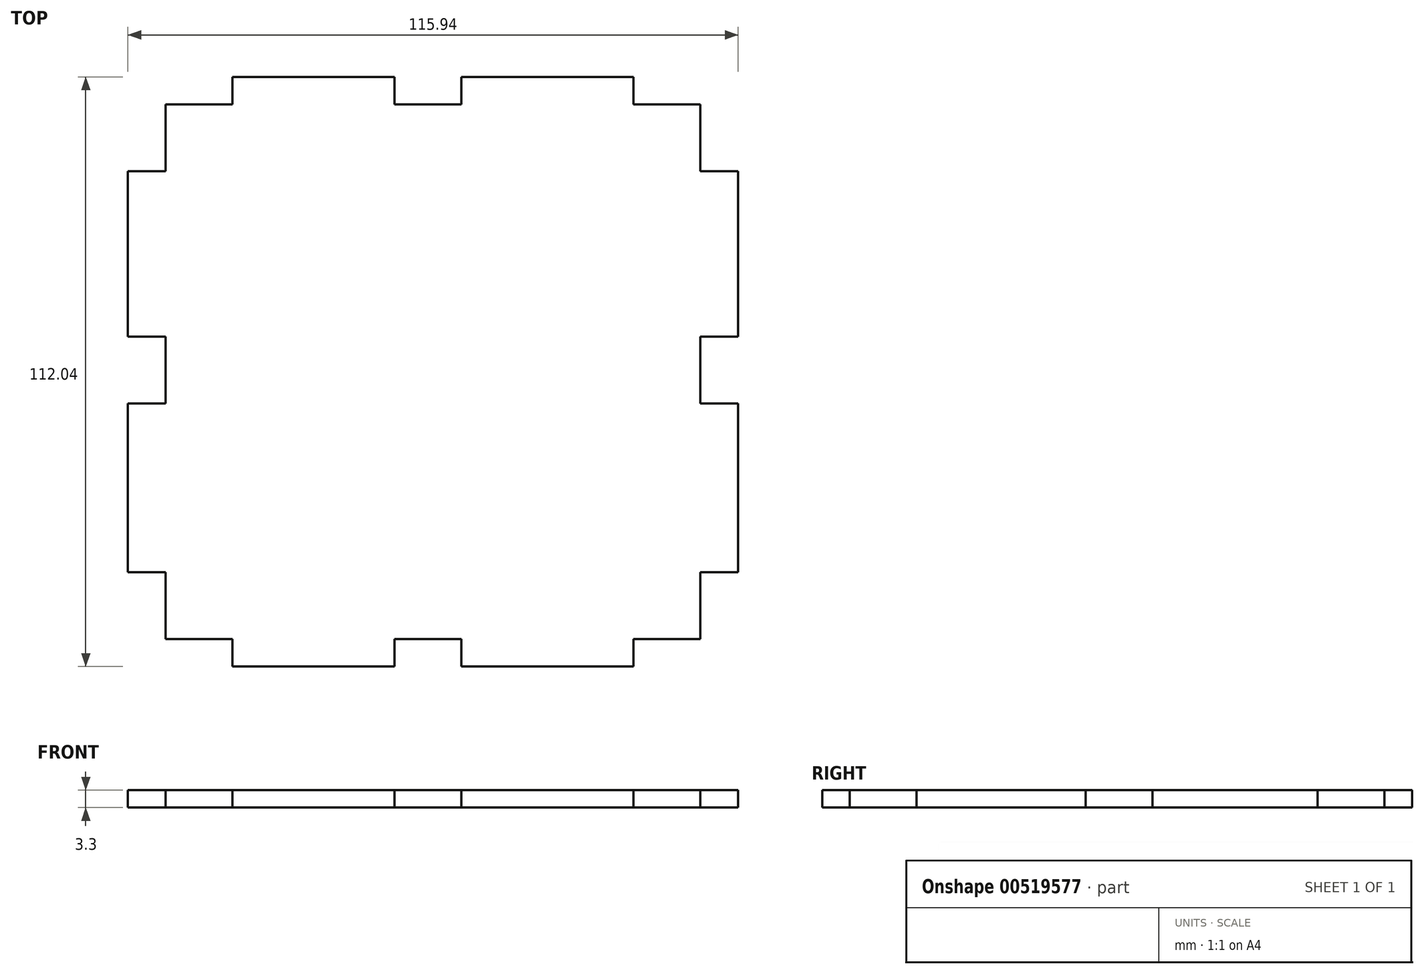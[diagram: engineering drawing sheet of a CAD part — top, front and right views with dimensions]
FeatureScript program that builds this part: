
annotation { "Feature Type Name" : "Feature", "Feature Type Description" : "" }
export const myFeature = defineFeature(function(context is Context, id is Id, definition is map)
    precondition{}
    {
        {
            var Q0;
            Q0=qCreatedBy(makeId("Top.planeOp"),FACE);
            var sketch = newSketch(context, id + "F0", { "sketchPlane" : qUnion([Q0])});
            skLineSegment(sketch, "E0.bottom", {"start": v(50.8, -50.8) * mm, "end": v(38.1, -50.8) * mm});
            skLineSegment(sketch, "E0.top", {"start": v(50.8, 50.8) * mm, "end": v(38.1, 50.8) * mm});
            skLineSegment(sketch, "E0.left", {"start": v(50.8, -50.8) * mm, "end": v(50.8, -38.1) * mm});
            skLineSegment(sketch, "E0.right", {"start": v(-50.8, -50.8) * mm, "end": v(-50.8, -38.1) * mm});
            skPoint(sketch, "E0.middle", {"position": v(0, 0) * mm});
            skLineSegment(sketch, "E1", {"start": v(-50.8, 50.8) * mm, "end": v(-50.8, 56.02) * mm, "construction": true});
            skLineSegment(sketch, "E2", {"start": v(-50.8, 56.02) * mm, "end": v(-38.1, 56.02) * mm, "construction": true});
            skLineSegment(sketch, "E3", {"start": v(-38.1, 56.02) * mm, "end": v(-38.1, 50.8) * mm, "construction": true});
            skLineSegment(sketch, "E4", {"start": v(-38.1, 56.02) * mm, "end": v(-7.3, 56.02) * mm});
            skLineSegment(sketch, "E5", {"start": v(-38.1, 56.02) * mm, "end": v(-38.1, 50.8) * mm});
            skLineSegment(sketch, "E6", {"start": v(-7.3, 56.02) * mm, "end": v(-7.3, 50.8) * mm});
            skLineSegment(sketch, "E7.trimOffspring", {"start": v(-38.1, 50.8) * mm, "end": v(-50.8, 50.8) * mm});
            skLineSegment(sketch, "E8.MirrorCS", {"start": v(-38.1, -56.02) * mm, "end": v(-7.3, -56.02) * mm});
            skLineSegment(sketch, "E9.MirrorCS", {"start": v(-38.1, -56.02) * mm, "end": v(-38.1, -50.8) * mm});
            skLineSegment(sketch, "E10.MirrorCS", {"start": v(-7.3, -56.02) * mm, "end": v(-7.3, -50.8) * mm});
            skLineSegment(sketch, "E11.trimOffspring", {"start": v(-38.1, -50.8) * mm, "end": v(-50.8, -50.8) * mm});
            skLineSegment(sketch, "E12", {"start": v(-7.3, 56.02) * mm, "end": v(5.4, 56.02) * mm, "construction": true});
            skLineSegment(sketch, "E13", {"start": v(5.4, 56.02) * mm, "end": v(5.4, 50.8) * mm});
            skLineSegment(sketch, "E14", {"start": v(5.4, 56.02) * mm, "end": v(38.1, 56.02) * mm});
            skLineSegment(sketch, "E15", {"start": v(38.1, 56.02) * mm, "end": v(38.1, 50.8) * mm});
            skLineSegment(sketch, "E16.trimOffspring", {"start": v(5.4, 50.8) * mm, "end": v(-7.3, 50.8) * mm});
            skLineSegment(sketch, "E17.MirrorCS", {"start": v(5.4, -56.02) * mm, "end": v(5.4, -50.8) * mm});
            skLineSegment(sketch, "E18.MirrorCS", {"start": v(5.4, -56.02) * mm, "end": v(38.1, -56.02) * mm});
            skLineSegment(sketch, "E19.MirrorCS", {"start": v(38.1, -56.02) * mm, "end": v(38.1, -50.8) * mm});
            skLineSegment(sketch, "E20.trimOffspring", {"start": v(5.4, -50.8) * mm, "end": v(-7.3, -50.8) * mm});
            skLineSegment(sketch, "E21", {"start": v(-50.8, 0) * mm, "end": v(50.8, 0) * mm, "construction": true});
            skLineSegment(sketch, "E22", {"start": v(-50.8, 50.8) * mm, "end": v(-57.97, 50.8) * mm, "construction": true});
            skLineSegment(sketch, "E23", {"start": v(-57.97, 50.8) * mm, "end": v(-57.97, 38.1) * mm, "construction": true});
            skLineSegment(sketch, "E24", {"start": v(-50.8, 38.1) * mm, "end": v(-57.97, 38.1) * mm});
            skLineSegment(sketch, "E25", {"start": v(-57.97, 38.1) * mm, "end": v(-57.97, 6.7) * mm});
            skLineSegment(sketch, "E26", {"start": v(-57.97, 6.7) * mm, "end": v(-50.8, 6.7) * mm});
            skLineSegment(sketch, "E27.trimOffspring", {"start": v(-50.8, 38.1) * mm, "end": v(-50.8, 50.8) * mm});
            skLineSegment(sketch, "E28", {"start": v(-57.97, 6.7) * mm, "end": v(-57.97, -6) * mm, "construction": true});
            skLineSegment(sketch, "E29", {"start": v(-50.8, -6) * mm, "end": v(-57.97, -6) * mm});
            skLineSegment(sketch, "E30", {"start": v(-57.97, -6) * mm, "end": v(-57.97, -38.1) * mm});
            skLineSegment(sketch, "E31", {"start": v(-57.97, -38.1) * mm, "end": v(-50.8, -38.1) * mm});
            skLineSegment(sketch, "E32.MirrorCS", {"start": v(50.8, -6) * mm, "end": v(57.97, -6) * mm});
            skLineSegment(sketch, "E33.MirrorCS", {"start": v(57.97, -6) * mm, "end": v(57.97, -38.1) * mm});
            skLineSegment(sketch, "E34.MirrorCS", {"start": v(57.97, -38.1) * mm, "end": v(50.8, -38.1) * mm});
            skLineSegment(sketch, "E35.MirrorCS", {"start": v(57.97, 38.1) * mm, "end": v(57.97, 6.7) * mm});
            skLineSegment(sketch, "E36.MirrorCS", {"start": v(57.97, 6.7) * mm, "end": v(50.8, 6.7) * mm});
            skLineSegment(sketch, "E37.MirrorCS", {"start": v(50.8, 38.1) * mm, "end": v(57.97, 38.1) * mm});
            skLineSegment(sketch, "E38.trimOffspring", {"start": v(-50.8, -6) * mm, "end": v(-50.8, 6.7) * mm});
            skLineSegment(sketch, "E39.trimOffspring", {"start": v(50.8, 38.1) * mm, "end": v(50.8, 50.8) * mm});
            skLineSegment(sketch, "E40.trimOffspring", {"start": v(50.8, -6) * mm, "end": v(50.8, 6.7) * mm});
            skSolve(sketch);
        }
        {
            var Q0;
            Q0=makeQuery(id+"F0.imprint","IMPRINT",FACE,{"disambiguationData":[TD([[makeQuery(id+"F0.imprint","IMPRINT",EDGE,{"derivedFrom":sQuery(id+"F0.wireOp",EDGE,"E0.bottom")}),-1.0]])]});
            extrude(context, id + "F1", {"entities" : qUnion([Q0]), "depth" : 3.3 * mm, "offsetDistance" : 25.4 * mm});
        }
    });
